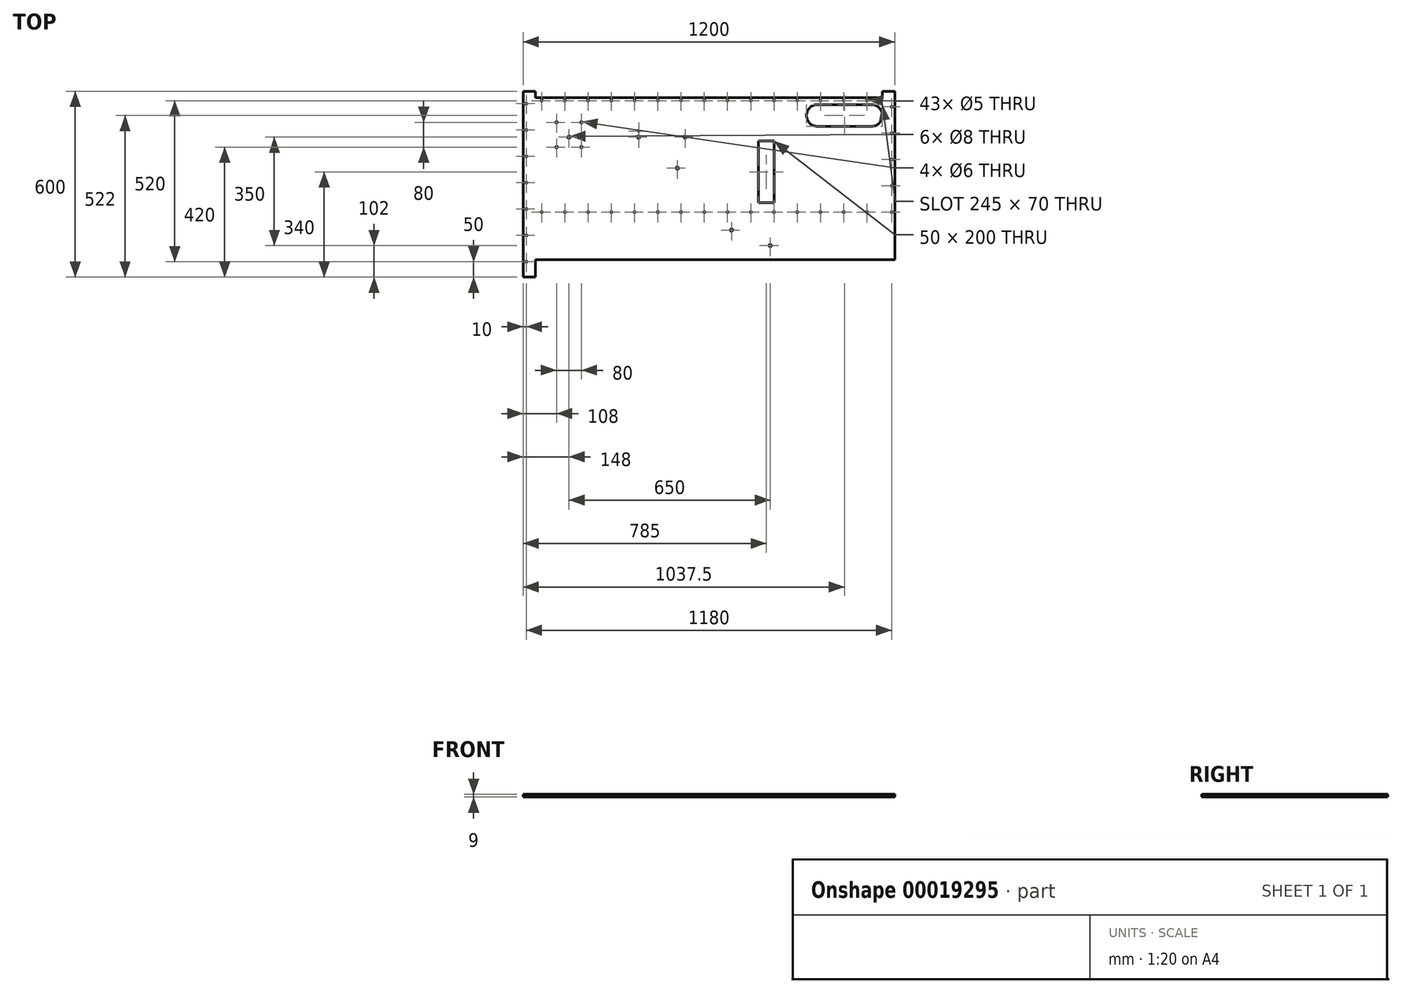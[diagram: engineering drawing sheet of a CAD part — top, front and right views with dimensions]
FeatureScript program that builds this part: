
annotation { "Feature Type Name" : "Feature", "Feature Type Description" : "" }
export const myFeature = defineFeature(function(context is Context, id is Id, definition is map)
    precondition{}
    {
        {
            var Q0;
            Q0=qCreatedBy(makeId("Top.planeOp"),FACE);
            var sketch = newSketch(context, id + "F0", { "sketchPlane" : qUnion([Q0])});
            skLineSegment(sketch, "E0.bottom", {"start": v(-600, 300) * mm, "end": v(600, 300) * mm, "construction": true});
            skLineSegment(sketch, "E0.top", {"start": v(-600, -300) * mm, "end": v(600, -300) * mm});
            skLineSegment(sketch, "E0.left", {"start": v(-600, 300) * mm, "end": v(-600, -300) * mm});
            skLineSegment(sketch, "E0.right", {"start": v(600, 300) * mm, "end": v(600, -300) * mm});
            skLineSegment(sketch, "E1", {"start": v(-600, 0) * mm, "end": v(600, 0) * mm, "construction": true});
            skCircle(sketch, "E2", {"center": v(-452, 152) * mm, "radius": 100 * mm, "construction": true});
            skCircle(sketch, "E3", {"center": v(-452, 152) * mm, "radius": 4 * mm});
            skArc(sketch, "E4", {"start": v(600, 0) * mm, "mid": v(450, -150) * mm, "end": v(600, -300) * mm, "construction": true});
            skArc(sketch, "E5", {"start": v(350, 257) * mm, "mid": v(315, 222) * mm, "end": v(350, 187) * mm});
            skArc(sketch, "E6", {"start": v(525, 187) * mm, "mid": v(560, 222) * mm, "end": v(525, 257) * mm});
            skLineSegment(sketch, "E7", {"start": v(350, 257) * mm, "end": v(525, 257) * mm});
            skLineSegment(sketch, "E8", {"start": v(525, 187) * mm, "end": v(350, 187) * mm});
            skLineSegment(sketch, "E9", {"start": v(-600, 270) * mm, "end": v(600, 270) * mm, "construction": true});
            skLineSegment(sketch, "E10", {"start": v(-590, 300) * mm, "end": v(-590, -300) * mm, "construction": true});
            skLineSegment(sketch, "E11", {"start": v(-600, -90) * mm, "end": v(600, -90) * mm, "construction": true});
            skCircle(sketch, "E12", {"center": v(-540, 270) * mm, "radius": 2.5 * mm});
            skCircle(sketch, "E13.1.0.0", {"center": v(-465, 270) * mm, "radius": 2.5 * mm});
            skCircle(sketch, "E13.2.0.0", {"center": v(-390, 270) * mm, "radius": 2.5 * mm});
            skCircle(sketch, "E13.3.0.0", {"center": v(-315, 270) * mm, "radius": 2.5 * mm});
            skCircle(sketch, "E13.4.0.0", {"center": v(-240, 270) * mm, "radius": 2.5 * mm});
            skCircle(sketch, "E13.5.0.0", {"center": v(-165, 270) * mm, "radius": 2.5 * mm});
            skCircle(sketch, "E13.6.0.0", {"center": v(-90, 270) * mm, "radius": 2.5 * mm});
            skCircle(sketch, "E13.7.0.0", {"center": v(-15, 270) * mm, "radius": 2.5 * mm});
            skCircle(sketch, "E13.8.0.0", {"center": v(60, 270) * mm, "radius": 2.5 * mm});
            skCircle(sketch, "E13.9.0.0", {"center": v(135, 270) * mm, "radius": 2.5 * mm});
            skCircle(sketch, "E13.10.0.0", {"center": v(210, 270) * mm, "radius": 2.5 * mm});
            skCircle(sketch, "E13.11.0.0", {"center": v(285, 270) * mm, "radius": 2.5 * mm});
            skCircle(sketch, "E13.12.0.0", {"center": v(360, 270) * mm, "radius": 2.5 * mm});
            skCircle(sketch, "E13.13.0.0", {"center": v(435, 270) * mm, "radius": 2.5 * mm});
            skCircle(sketch, "E13.14.0.0", {"center": v(510, 270) * mm, "radius": 2.5 * mm});
            skLineSegment(sketch, "E13.direction1", {"start": v(-540, 270) * mm, "end": v(-465, 270) * mm, "construction": true});
            skCircle(sketch, "E14", {"center": v(-540, -90) * mm, "radius": 2.5 * mm});
            skCircle(sketch, "E15.1.0.0", {"center": v(-465, -90) * mm, "radius": 2.5 * mm});
            skCircle(sketch, "E15.2.0.0", {"center": v(-390, -90) * mm, "radius": 2.5 * mm});
            skLineSegment(sketch, "E15.direction1", {"start": v(-540, -90) * mm, "end": v(-465, -90) * mm, "construction": true});
            skCircle(sketch, "E16.0.3.0", {"center": v(-315, -90) * mm, "radius": 2.5 * mm});
            skCircle(sketch, "E16.0.4.0", {"center": v(-240, -90) * mm, "radius": 2.5 * mm});
            skCircle(sketch, "E16.0.5.0", {"center": v(-165, -90) * mm, "radius": 2.5 * mm});
            skCircle(sketch, "E16.0.6.0", {"center": v(-90, -90) * mm, "radius": 2.5 * mm});
            skCircle(sketch, "E16.0.7.0", {"center": v(-15, -90) * mm, "radius": 2.5 * mm});
            skCircle(sketch, "E16.0.8.0", {"center": v(60, -90) * mm, "radius": 2.5 * mm});
            skCircle(sketch, "E16.0.9.0", {"center": v(135, -90) * mm, "radius": 2.5 * mm});
            skCircle(sketch, "E16.0.10.0", {"center": v(210, -90) * mm, "radius": 2.5 * mm});
            skCircle(sketch, "E16.0.11.0", {"center": v(285, -90) * mm, "radius": 2.5 * mm});
            skCircle(sketch, "E16.0.12.0", {"center": v(360, -90) * mm, "radius": 2.5 * mm});
            skCircle(sketch, "E16.0.13.0", {"center": v(435, -90) * mm, "radius": 2.5 * mm});
            skCircle(sketch, "E16.0.14.0", {"center": v(510, -90) * mm, "radius": 2.5 * mm});
            skCircle(sketch, "E17", {"center": v(-590, -250) * mm, "radius": 2.5 * mm});
            skCircle(sketch, "E18.0.1.0", {"center": v(-590, -165) * mm, "radius": 2.5 * mm});
            skCircle(sketch, "E18.0.2.0", {"center": v(-590, -80) * mm, "radius": 2.5 * mm});
            skCircle(sketch, "E18.0.3.0", {"center": v(-590, 5) * mm, "radius": 2.5 * mm});
            skCircle(sketch, "E18.0.4.0", {"center": v(-590, 90) * mm, "radius": 2.5 * mm});
            skCircle(sketch, "E18.0.5.0", {"center": v(-590, 175) * mm, "radius": 2.5 * mm});
            skCircle(sketch, "E18.0.6.0", {"center": v(-590, 260) * mm, "radius": 2.5 * mm});
            skLineSegment(sketch, "E18.direction1", {"start": v(-590, -250) * mm, "end": v(-565, -250) * mm, "construction": true});
            skLineSegment(sketch, "E18.direction2", {"start": v(-590, -250) * mm, "end": v(-590, -165) * mm, "construction": true});
            skLineSegment(sketch, "E19", {"start": v(590, -300) * mm, "end": v(590, 300) * mm, "construction": true});
            skCircle(sketch, "E20", {"center": v(590, 250) * mm, "radius": 2.5 * mm});
            skCircle(sketch, "E21.0.1.0", {"center": v(590, 165) * mm, "radius": 2.5 * mm});
            skCircle(sketch, "E21.0.2.0", {"center": v(590, 80) * mm, "radius": 2.5 * mm});
            skCircle(sketch, "E21.0.3.0", {"center": v(590, -5) * mm, "radius": 2.5 * mm});
            skCircle(sketch, "E21.0.4.0", {"center": v(590, -90) * mm, "radius": 2.5 * mm});
            skLineSegment(sketch, "E21.direction1", {"start": v(590, 250) * mm, "end": v(615, 250) * mm, "construction": true});
            skLineSegment(sketch, "E21.direction2", {"start": v(590, 250) * mm, "end": v(590, 165) * mm, "construction": true});
            skLineSegment(sketch, "E22", {"start": v(-600, 300) * mm, "end": v(-560, 300) * mm});
            skLineSegment(sketch, "E23", {"start": v(-560, 300) * mm, "end": v(-560, 280) * mm});
            skLineSegment(sketch, "E24", {"start": v(-560, 280) * mm, "end": v(560, 280) * mm});
            skLineSegment(sketch, "E25", {"start": v(560, 280) * mm, "end": v(560, 300) * mm});
            skLineSegment(sketch, "E26", {"start": v(560, 300) * mm, "end": v(600, 300) * mm});
            skSolve(sketch);
        }
        {
            var Q0;
            Q0=qSketchRegion(id+"F0",true);
            extrude(context, id + "F1", {"entities" : qUnion([Q0]), "depth" : 9 * mm});
        }
        {
            var Q0;
            Q0=makeQuery(id+"F1.opExtrude","CAP_FACE",FACE,{"disambiguationData":[OSD([sQuery(id+"F0.wireOp",EDGE,"E0.bottom"),sQuery(id+"F0.wireOp",EDGE,"E0.top"),sQuery(id+"F0.wireOp",EDGE,"E0.left"),sQuery(id+"F0.wireOp",EDGE,"E0.right"),sQuery(id+"F0.wireOp",EDGE,"E3"),sQuery(id+"F0.wireOp",EDGE,"E5"),sQuery(id+"F0.wireOp",EDGE,"E6"),sQuery(id+"F0.wireOp",EDGE,"E7"),sQuery(id+"F0.wireOp",EDGE,"E8"),sQuery(id+"F0.wireOp",EDGE,"90365ca1-145e-49f4-b966-b2422279f9df"),sQuery(id+"F0.wireOp",EDGE,"54d5aa8c-19b3-4af9-a89f-b2943a9900e4")])],"isStart":false});
            var sketch = newSketch(context, id + "F2", { "sketchPlane" : qUnion([Q0])});
            skCircle(sketch, "E27.0", {"center": v(-452, 152) * mm, "radius": 4 * mm});
            skLineSegment(sketch, "E28.bottom", {"start": v(160, 140) * mm, "end": v(210, 140) * mm});
            skLineSegment(sketch, "E28.top", {"start": v(160, -60) * mm, "end": v(210, -60) * mm});
            skLineSegment(sketch, "E28.left", {"start": v(160, 140) * mm, "end": v(160, -60) * mm});
            skLineSegment(sketch, "E28.right", {"start": v(210, 140) * mm, "end": v(210, -60) * mm});
            skLineSegment(sketch, "E29.direction1", {"start": v(-452, 152) * mm, "end": v(-427, 152) * mm, "construction": true});
            skLineSegment(sketch, "E29.direction2", {"start": v(-452, 152) * mm, "end": v(-452, 127) * mm, "construction": true});
            skCircle(sketch, "E30.0.8.0", {"center": v(-227, 152) * mm, "radius": 4 * mm});
            skCircle(sketch, "E30.0.15.0", {"center": v(-77, 152) * mm, "radius": 4 * mm});
            skCircle(sketch, "E31.0.15.3", {"center": v(-102, 52) * mm, "radius": 4 * mm});
            skCircle(sketch, "E31.0.21.11", {"center": v(73, -148) * mm, "radius": 4 * mm});
            skCircle(sketch, "E31.0.26.14", {"center": v(198, -198) * mm, "radius": 4 * mm});
            skLineSegment(sketch, "E32", {"start": v(-560, -300) * mm, "end": v(-560, -244) * mm});
            skLineSegment(sketch, "E33", {"start": v(-560, -244) * mm, "end": v(600, -244) * mm});
            skLineSegment(sketch, "E34", {"start": v(600, -244) * mm, "end": v(600, -300) * mm});
            skLineSegment(sketch, "E35", {"start": v(600, -300) * mm, "end": v(-560, -300) * mm});
            skCircle(sketch, "E36", {"center": v(-227, 172) * mm, "radius": 2.5 * mm});
            skSolve(sketch);
        }
        {
            var Q0;
            Q0=qSketchRegion(id+"F2",true);
            extrude(context, id + "F3", {"entities" : qUnion([Q0]), "operationType" : NewBodyOperationType.REMOVE, "oppositeDirection" : true, "depth" : 25 * mm});
        }
        {
            var Q0;
            Q0=makeQuery(id+"F1.opExtrude","CAP_FACE",FACE,{"disambiguationData":[OSD([sQuery(id+"F0.wireOp",EDGE,"E0.bottom"),sQuery(id+"F0.wireOp",EDGE,"E0.top"),sQuery(id+"F0.wireOp",EDGE,"E0.left"),sQuery(id+"F0.wireOp",EDGE,"E0.right"),sQuery(id+"F0.wireOp",EDGE,"E3"),sQuery(id+"F0.wireOp",EDGE,"E5"),sQuery(id+"F0.wireOp",EDGE,"E6"),sQuery(id+"F0.wireOp",EDGE,"E7"),sQuery(id+"F0.wireOp",EDGE,"E8"),sQuery(id+"F0.wireOp",EDGE,"E12"),sQuery(id+"F0.wireOp",EDGE,"E13.1.0.0"),sQuery(id+"F0.wireOp",EDGE,"E13.2.0.0"),sQuery(id+"F0.wireOp",EDGE,"E13.3.0.0"),sQuery(id+"F0.wireOp",EDGE,"E13.4.0.0"),sQuery(id+"F0.wireOp",EDGE,"E13.5.0.0"),sQuery(id+"F0.wireOp",EDGE,"E13.6.0.0"),sQuery(id+"F0.wireOp",EDGE,"E13.7.0.0"),sQuery(id+"F0.wireOp",EDGE,"E13.8.0.0"),sQuery(id+"F0.wireOp",EDGE,"E13.9.0.0"),sQuery(id+"F0.wireOp",EDGE,"E13.10.0.0"),sQuery(id+"F0.wireOp",EDGE,"E13.11.0.0"),sQuery(id+"F0.wireOp",EDGE,"E13.12.0.0"),sQuery(id+"F0.wireOp",EDGE,"E13.13.0.0"),sQuery(id+"F0.wireOp",EDGE,"E13.14.0.0"),sQuery(id+"F0.wireOp",EDGE,"E14"),sQuery(id+"F0.wireOp",EDGE,"E15.1.0.0"),sQuery(id+"F0.wireOp",EDGE,"E15.2.0.0"),sQuery(id+"F0.wireOp",EDGE,"E16.0.3.0"),sQuery(id+"F0.wireOp",EDGE,"E16.0.4.0"),sQuery(id+"F0.wireOp",EDGE,"E16.0.5.0"),sQuery(id+"F0.wireOp",EDGE,"E16.0.6.0"),sQuery(id+"F0.wireOp",EDGE,"E16.0.7.0"),sQuery(id+"F0.wireOp",EDGE,"E16.0.8.0"),sQuery(id+"F0.wireOp",EDGE,"E16.0.9.0"),sQuery(id+"F0.wireOp",EDGE,"E16.0.10.0"),sQuery(id+"F0.wireOp",EDGE,"E16.0.11.0"),sQuery(id+"F0.wireOp",EDGE,"E16.0.12.0"),sQuery(id+"F0.wireOp",EDGE,"E16.0.13.0"),sQuery(id+"F0.wireOp",EDGE,"E16.0.14.0")])],"isStart":false});
            var sketch = newSketch(context, id + "F4", { "sketchPlane" : qUnion([Q0])});
            skLineSegment(sketch, "E37.bottom", {"start": v(-492, 200) * mm, "end": v(-412, 200) * mm, "construction": true});
            skLineSegment(sketch, "E37.top", {"start": v(-492, 120) * mm, "end": v(-412, 120) * mm, "construction": true});
            skLineSegment(sketch, "E37.left", {"start": v(-492, 200) * mm, "end": v(-492, 120) * mm, "construction": true});
            skLineSegment(sketch, "E37.right", {"start": v(-412, 200) * mm, "end": v(-412, 120) * mm, "construction": true});
            skCircle(sketch, "E38", {"center": v(-492, 200) * mm, "radius": 3 * mm});
            skCircle(sketch, "E39", {"center": v(-412, 200) * mm, "radius": 3 * mm});
            skCircle(sketch, "E40", {"center": v(-492, 120) * mm, "radius": 3 * mm});
            skCircle(sketch, "E41", {"center": v(-412, 120) * mm, "radius": 3 * mm});
            skLineSegment(sketch, "E42", {"start": v(-452, 200) * mm, "end": v(-452, 120) * mm, "construction": true});
            skLineSegment(sketch, "E43", {"start": v(-492, 152) * mm, "end": v(-412, 152) * mm, "construction": true});
            skPoint(sketch, "E44", {"position": v(-452, 152) * mm});
            skLineSegment(sketch, "E45", {"start": v(-600, -90) * mm, "end": v(600, -90) * mm, "construction": true});
            skPoint(sketch, "E46", {"position": v(-390, -90) * mm});
            skSolve(sketch);
        }
        {
            var Q0;
            Q0=qSketchRegion(id+"F4",true);
            extrude(context, id + "F5", {"entities" : qUnion([Q0]), "operationType" : NewBodyOperationType.REMOVE, "oppositeDirection" : true, "depth" : 25 * mm});
        }
    });
